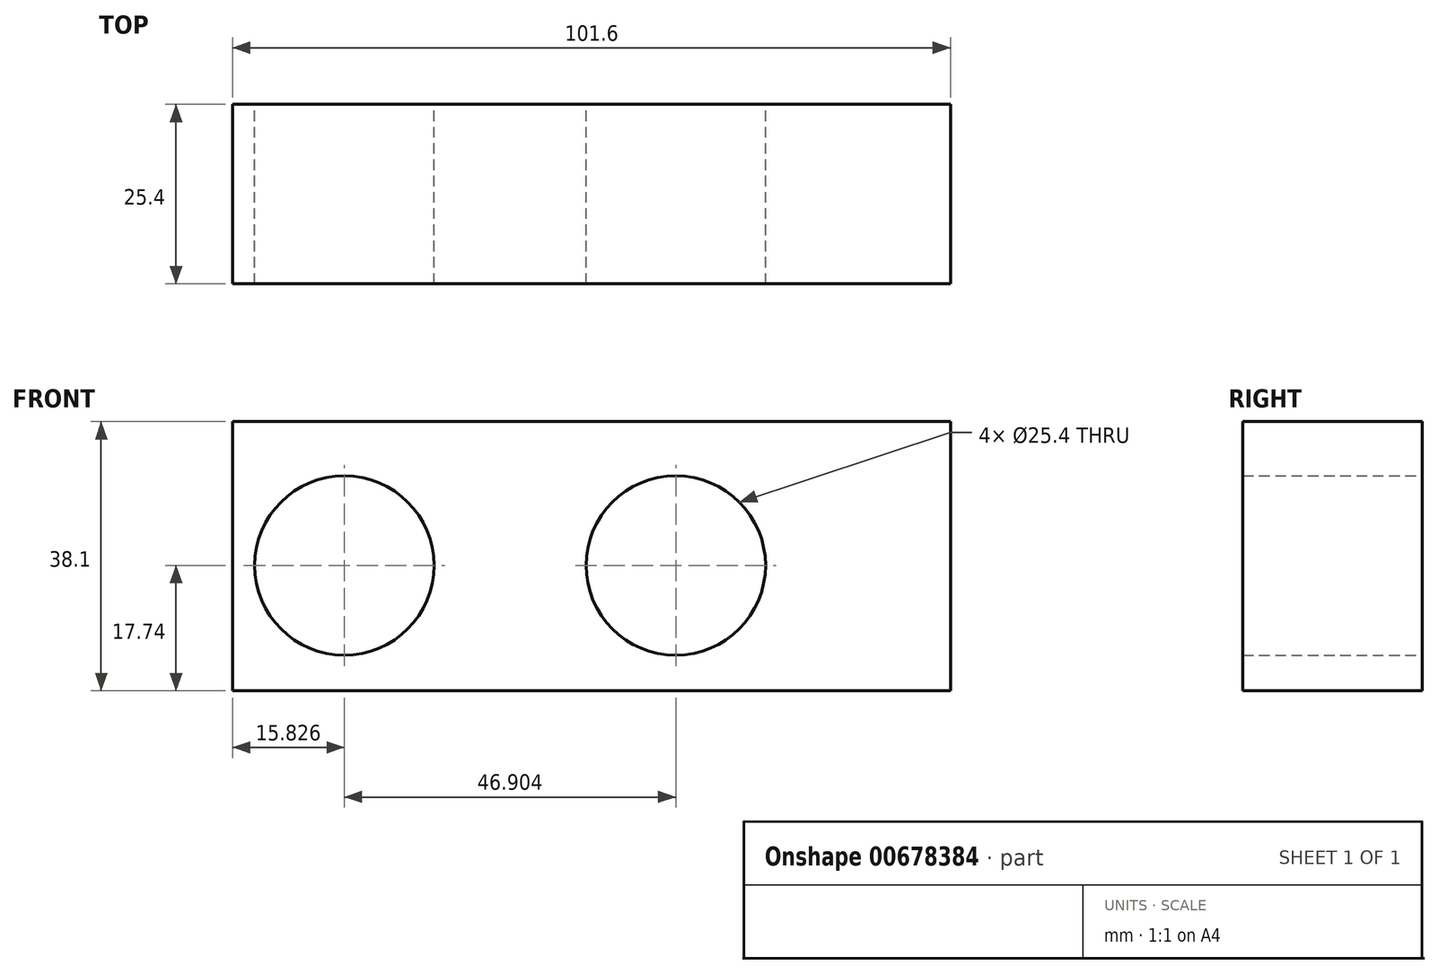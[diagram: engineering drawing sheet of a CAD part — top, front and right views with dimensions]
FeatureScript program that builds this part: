
annotation { "Feature Type Name" : "Feature", "Feature Type Description" : "" }
export const myFeature = defineFeature(function(context is Context, id is Id, definition is map)
    precondition{}
    {
        {
            var Q0;
            Q0=qCreatedBy(makeId("Front.planeOp"),FACE);
            var sketch = newSketch(context, id + "F0", { "sketchPlane" : qUnion([Q0])});
            skCircle(sketch, "E0", {"center": v(0, 0) * mm, "radius": 12.7 * mm});
            skLineSegment(sketch, "E1.bottom", {"start": v(38.87, 20.36) * mm, "end": v(-62.73, 20.36) * mm});
            skLineSegment(sketch, "E1.top", {"start": v(38.87, -17.74) * mm, "end": v(-62.73, -17.74) * mm});
            skLineSegment(sketch, "E1.left", {"start": v(38.87, 20.36) * mm, "end": v(38.87, -17.74) * mm});
            skLineSegment(sketch, "E1.right", {"start": v(-62.73, 20.36) * mm, "end": v(-62.73, -17.74) * mm});
            skCircle(sketch, "E2", {"center": v(-46.9, 0) * mm, "radius": 12.7 * mm});
            skSolve(sketch);
        }
        {
            var Q0;
            Q0 = qSketchRegion(id + "F0", true);
            extrude(context, id + "F1", {"entities" : qUnion([Q0]), "depth" : 25.4 * mm, "offsetDistance" : 25.4 * mm});
        }
    });
